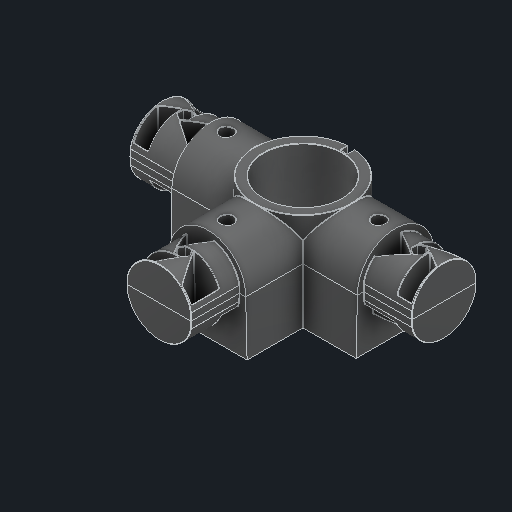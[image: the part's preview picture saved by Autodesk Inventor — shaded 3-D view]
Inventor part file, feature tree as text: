
AUTODESK INVENTOR PART (.ipt)
format: ipt  version: 2024 (Build 280153000, 153)  size: 4,863,488 bytes
history: native  units: in
note: dims shown in document units (in); Inventor stores cm internally (conversion verified against a paired STEP export)
features: fillet x1
ambient origin geometry x8: Origin, YZ Plane, XZ Plane, XY Plane, X Axis, Y Axis, Z Axis, Center Point
bodies: Solid1 (feature_tree)
feature tree (1):
  fillet  "Fillet8"  [1 undecoded]
note: 1 required parameter value undecoded (feature->parameter linkage not recoverable at this tier; creation-order binding heuristic only, values carry confidence <= 0.55)
